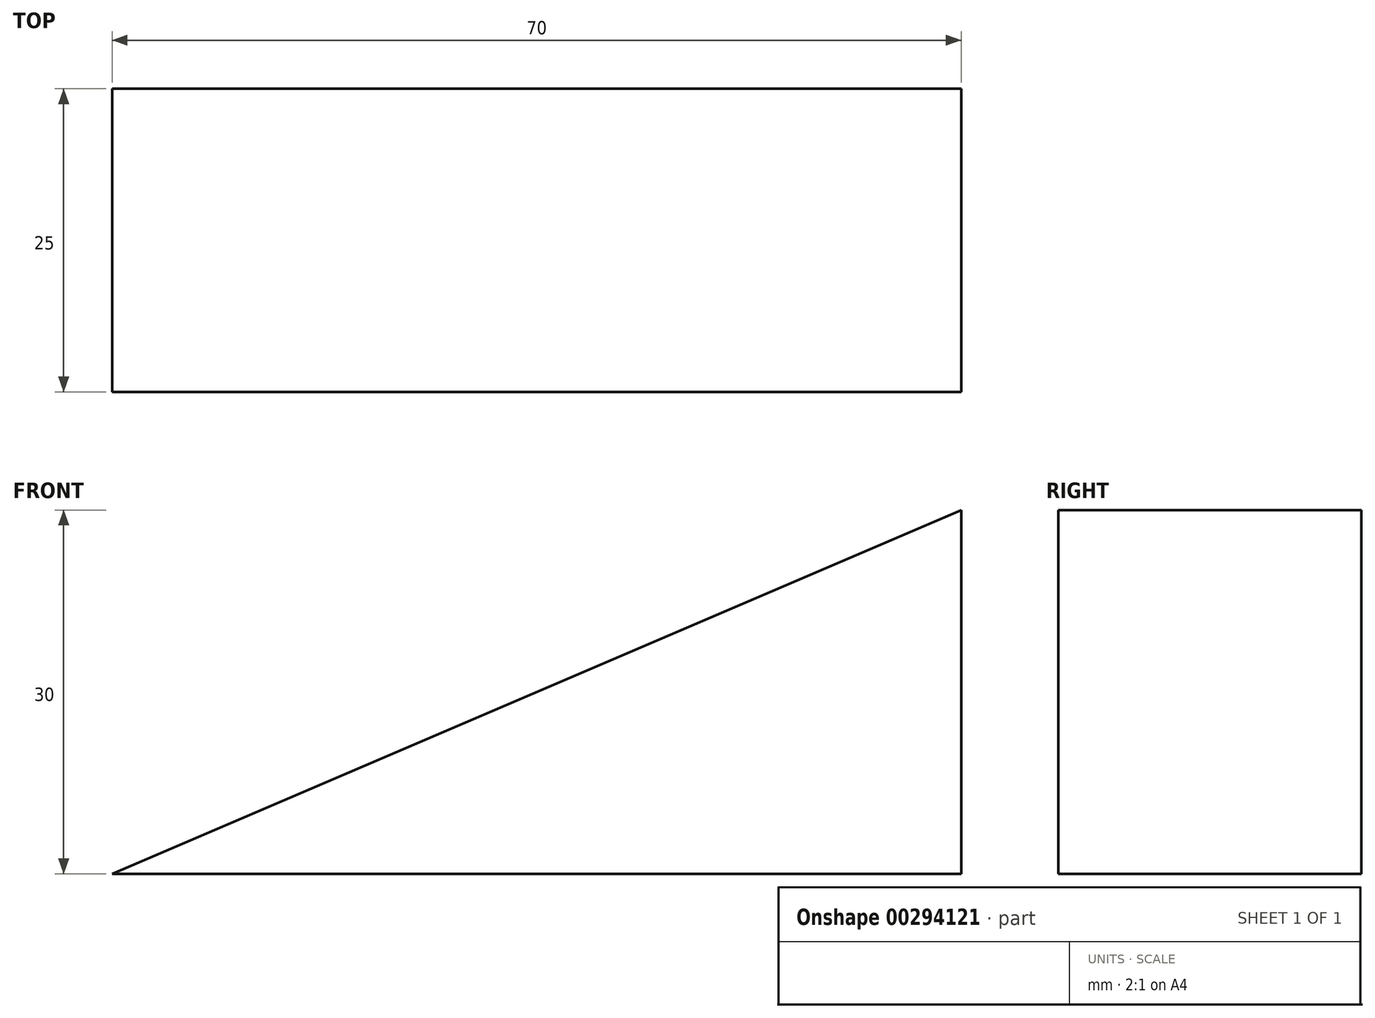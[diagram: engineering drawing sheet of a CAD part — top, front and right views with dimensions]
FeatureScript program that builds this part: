
annotation { "Feature Type Name" : "Feature", "Feature Type Description" : "" }
export const myFeature = defineFeature(function(context is Context, id is Id, definition is map)
    precondition{}
    {
        {
            var Q0;
            Q0=qCreatedBy(makeId("Front.planeOp"),FACE);
            var sketch = newSketch(context, id + "F0", { "sketchPlane" : qUnion([Q0])});
            skLineSegment(sketch, "E0", {"start": v(-38.66, 0) * mm, "end": v(31.34, 0) * mm});
            skLineSegment(sketch, "E1", {"start": v(31.34, 0) * mm, "end": v(31.34, 30) * mm});
            skLineSegment(sketch, "E2", {"start": v(31.34, 30) * mm, "end": v(-38.66, 0) * mm});
            skSolve(sketch);
        }
        {
            var Q0;
            Q0 = qSketchRegion(id + "F0", true);
            extrude(context, id + "F1", {"entities" : qUnion([Q0]), "depth" : 25 * mm});
        }
    });
